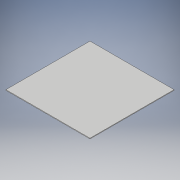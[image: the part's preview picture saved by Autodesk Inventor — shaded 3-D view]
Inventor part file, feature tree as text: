
AUTODESK INVENTOR PART (.ipt)
format: ipt  version: 2018 (Build 220112000, 112)  size: 90,112 bytes
history: native  units: in
note: dims shown in document units (in); Inventor stores cm internally (conversion verified against a paired STEP export)
features: extrude x1, sketch x1
ambient origin geometry x8: Origin, YZ Plane, XZ Plane, XY Plane, X Axis, Y Axis, Z Axis, Center Point
bodies: Solid1 (feature_tree)
feature tree (2):
  extrude  "Extrusion1"  Depth=3.937in
  sketch  "Sketch1"  dims[d0=3.937in d1=3.937in d2=0.031in d3=0.0in]
